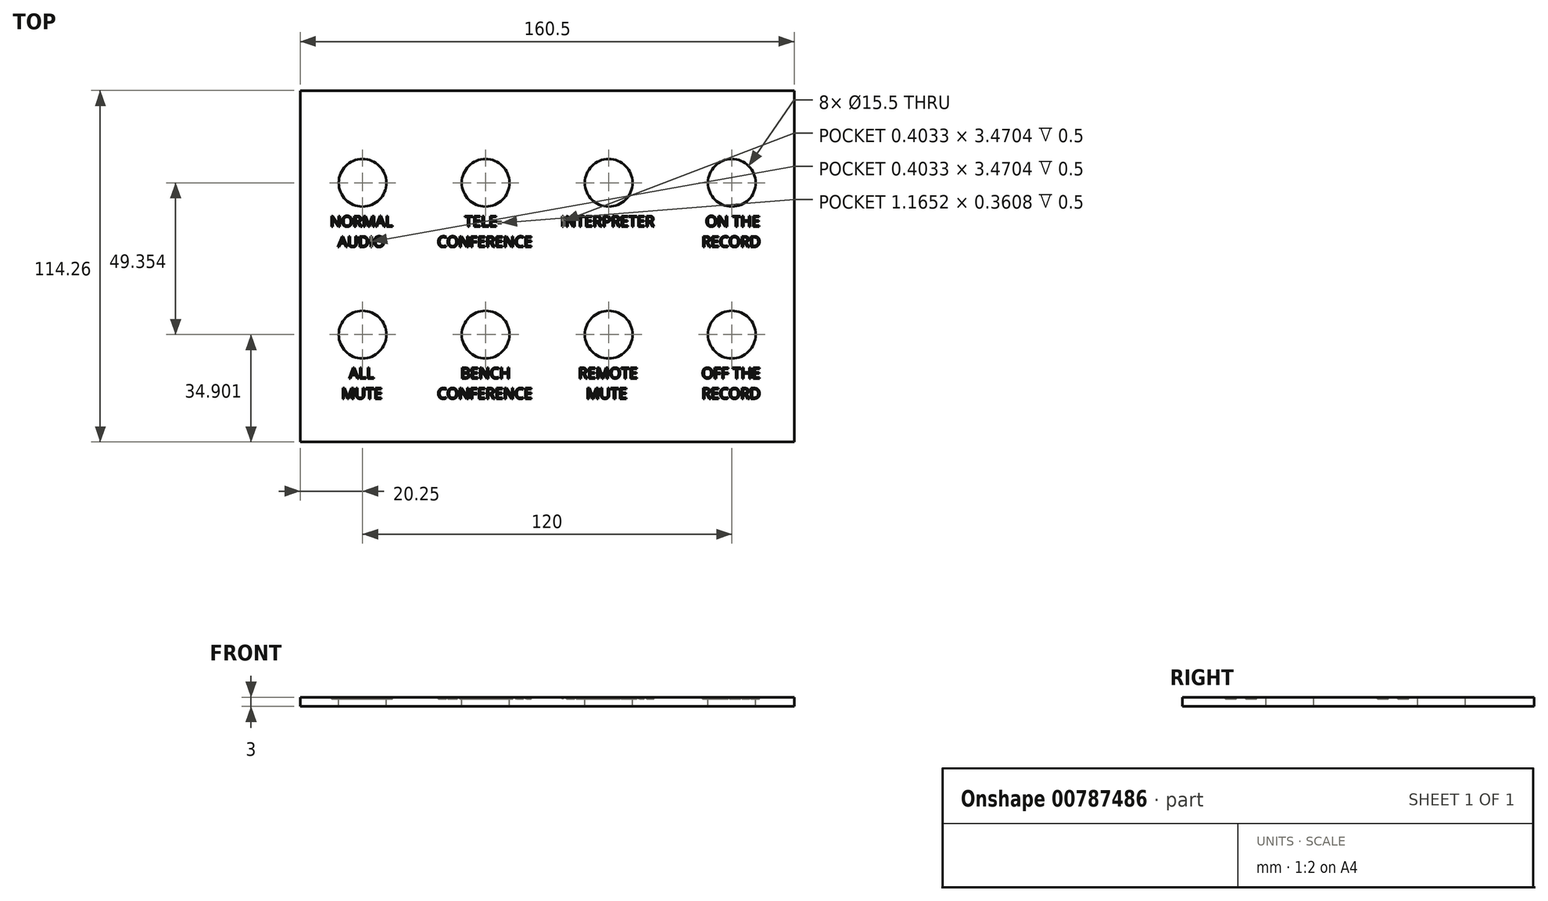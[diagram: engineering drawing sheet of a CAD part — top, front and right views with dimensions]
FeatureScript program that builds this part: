
annotation { "Feature Type Name" : "Feature", "Feature Type Description" : "" }
export const myFeature = defineFeature(function(context is Context, id is Id, definition is map)
    precondition{}
    {
        {
            var Q0;
            Q0=qCreatedBy(makeId("Top.planeOp"),FACE);
            var sketch = newSketch(context, id + "F0", { "sketchPlane" : qUnion([Q0])});
            skLineSegment(sketch, "E0.bottom", {"start": v(-80.25, 57.12) * mm, "end": v(80.25, 57.13) * mm});
            skLineSegment(sketch, "E0.top", {"start": v(-80.25, -57.13) * mm, "end": v(80.25, -57.12) * mm});
            skLineSegment(sketch, "E0.left", {"start": v(-80.25, 57.12) * mm, "end": v(-80.25, -57.13) * mm});
            skLineSegment(sketch, "E0.right", {"start": v(80.25, 57.13) * mm, "end": v(80.25, -57.12) * mm});
            skSolve(sketch);
        }
        {
            var Q0;
            Q0 = qSketchRegion(id + "F0", true);
            extrude(context, id + "F1", {"entities" : qUnion([Q0]), "depth" : 3 * mm, "offsetDistance" : 25 * mm});
        }
        {
            var Q0;
            Q0=makeQuery(id+"F1.opExtrude","CAP_FACE",FACE,{"disambiguationData":[OSD([sQuery(id+"F0.wireOp",EDGE,"E0.bottom"),sQuery(id+"F0.wireOp",EDGE,"E0.top"),sQuery(id+"F0.wireOp",EDGE,"E0.left"),sQuery(id+"F0.wireOp",EDGE,"E0.right")])],"isStart":false});
            var sketch = newSketch(context, id + "F2", { "sketchPlane" : qUnion([Q0])});
            skLineSegment(sketch, "E1", {"start": v(-60, 27.13) * mm, "end": v(60, 27.13) * mm, "construction": true});
            skLineSegment(sketch, "E2", {"start": v(-60, -22.23) * mm, "end": v(60, -22.23) * mm, "construction": true});
            skLineSegment(sketch, "E3", {"start": v(-20, 27.13) * mm, "end": v(-20, -22.23) * mm, "construction": true});
            skLineSegment(sketch, "E4", {"start": v(20, 27.13) * mm, "end": v(20, -22.23) * mm, "construction": true});
            skCircle(sketch, "E5", {"center": v(-60, 27.13) * mm, "radius": 7.75 * mm});
            skCircle(sketch, "E6", {"center": v(-20, 27.13) * mm, "radius": 7.75 * mm});
            skCircle(sketch, "E7", {"center": v(20, 27.13) * mm, "radius": 7.75 * mm});
            skCircle(sketch, "E8", {"center": v(60, 27.13) * mm, "radius": 7.75 * mm});
            skCircle(sketch, "E9", {"center": v(-60, -22.23) * mm, "radius": 7.75 * mm});
            skCircle(sketch, "E10", {"center": v(-20, -22.23) * mm, "radius": 7.75 * mm});
            skCircle(sketch, "E11", {"center": v(20, -22.23) * mm, "radius": 7.75 * mm});
            skCircle(sketch, "E12", {"center": v(60, -22.23) * mm, "radius": 7.75 * mm});
            skSolve(sketch);
        }
        {
            var Q0;
            Q0 = qSketchRegion(id + "F2", true);
            var Q1;
            Q1=makeQuery(id+"F1.opExtrude","CAP_FACE",FACE,{"disambiguationData":[OSD([sQuery(id+"F0.wireOp",EDGE,"E0.bottom"),sQuery(id+"F0.wireOp",EDGE,"E0.top"),sQuery(id+"F0.wireOp",EDGE,"E0.left"),sQuery(id+"F0.wireOp",EDGE,"E0.right")])],"isStart":true});
            extrude(context, id + "F3", {"entities" : qUnion([Q0]), "operationType" : NewBodyOperationType.REMOVE, "endBound" : BoundingType.UP_TO_SURFACE, "oppositeDirection" : true, "depth" : 25 * mm, "endBoundEntityFace" : qUnion([Q1]), "offsetDistance" : 25 * mm});
        }
        {
            var Q0;
            Q0=makeQuery(id+"F1.opExtrude","CAP_FACE",FACE,{"disambiguationData":[OSD([sQuery(id+"F0.wireOp",EDGE,"E0.bottom"),sQuery(id+"F0.wireOp",EDGE,"E0.top"),sQuery(id+"F0.wireOp",EDGE,"E0.left"),sQuery(id+"F0.wireOp",EDGE,"E0.right")])],"isStart":false});
            var sketch = newSketch(context, id + "F4", { "sketchPlane" : qUnion([Q0])});
            skText(sketch, "E13", { "text": "NORMAL\n  AUDIO", "fontName": "OpenSans-Regular.ttf"});
            skText(sketch, "E14", { "text": "       TELE-\nCONFERENCE", "fontName": "OpenSans-Regular.ttf"});
            skText(sketch, "E15", { "text": "INTERPRETER", "fontName": "OpenSans-Regular.ttf"});
            skText(sketch, "E16", { "text": " ON THE\nRECORD", "fontName": "OpenSans-Regular.ttf"});
            skText(sketch, "E17", { "text": "  ALL\nMUTE", "fontName": "OpenSans-Regular.ttf"});
            skText(sketch, "E18", { "text": "      BENCH\nCONFERENCE", "fontName": "OpenSans-Regular.ttf"});
            skText(sketch, "E19", { "text": "REMOTE\n  MUTE", "fontName": "OpenSans-Regular.ttf"});
            skText(sketch, "E20", { "text": "OFF THE\nRECORD", "fontName": "OpenSans-Regular.ttf"});
            const initialGuessF4  = {"E13": [-0.07057, 0.01288, 1, 0, 0.0035], "E14": [-0.0357, 0.01287, 1, 0, 0.0035], "E15": [0.0044, 0.01288, 1, 0, 0.0035], "E16": [0.05019, 0.01288, 1, 0, 0.0035], "E17": [-0.06692, -0.03648, 1, 0, 0.0035], "E18": [-0.0357, -0.03648, 1, 0, 0.0035], "E19": [0.0101, -0.03648, 1, 0, 0.0035], "E20": [0.05019, -0.03648, 1, 0, 0.0035]};
            skSetInitialGuess(sketch, initialGuessF4);
            skSolve(sketch);
        }
        {
            var Q0;
            Q0 = qSketchRegion(id + "F4", true);
            extrude(context, id + "F5", {"entities" : qUnion([Q0]), "operationType" : NewBodyOperationType.REMOVE, "oppositeDirection" : true, "depth" : 0.5 * mm, "offsetDistance" : 25 * mm});
        }
    });
